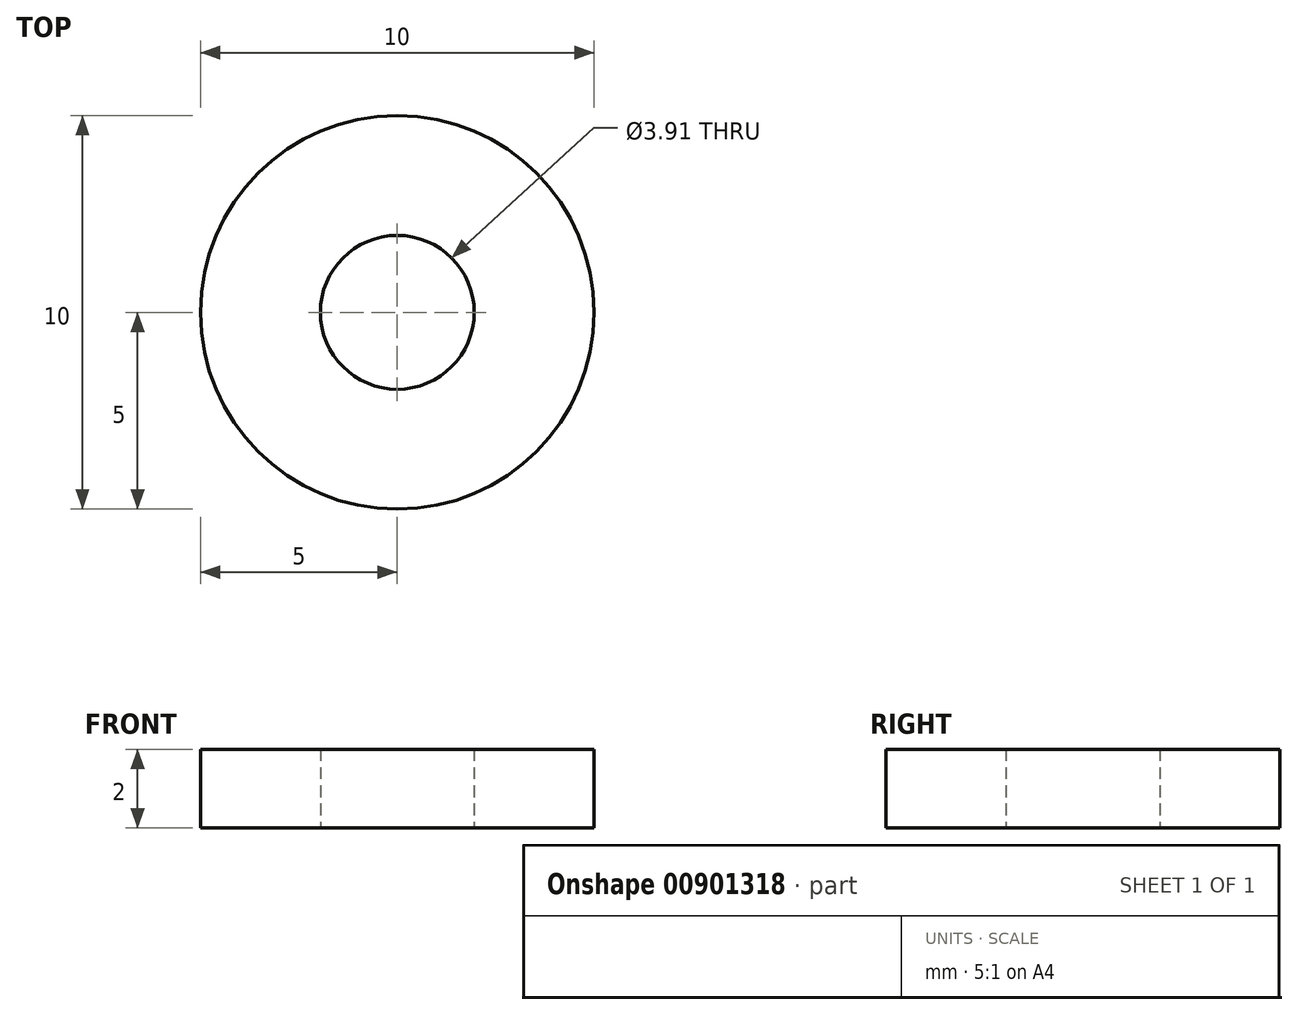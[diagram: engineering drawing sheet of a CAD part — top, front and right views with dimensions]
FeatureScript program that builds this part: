
annotation { "Feature Type Name" : "Feature", "Feature Type Description" : "" }
export const myFeature = defineFeature(function(context is Context, id is Id, definition is map)
    precondition{}
    {
        {
            var Q0;
            Q0=qCreatedBy(makeId("Top.planeOp"),FACE);
            var sketch = newSketch(context, id + "F0", { "sketchPlane" : qUnion([Q0])});
            skCircle(sketch, "E0", {"center": v(0, 0) * mm, "radius": 5 * mm});
            skCircle(sketch, "E1", {"center": v(0, 0) * mm, "radius": 1.96 * mm});
            skSolve(sketch);
        }
        {
            var Q0;
            Q0=makeQuery(id+"F0.imprint","IMPRINT",FACE,{"disambiguationData":[TD([[makeQuery(id+"F0.imprint","IMPRINT",EDGE,{"derivedFrom":sQuery(id+"F0.wireOp",EDGE,"E0")}),1.0]])]});
            extrude(context, id + "F1", {"entities" : qUnion([Q0]), "depth" : 2 * mm, "offsetDistance" : 25 * mm});
        }
    });
